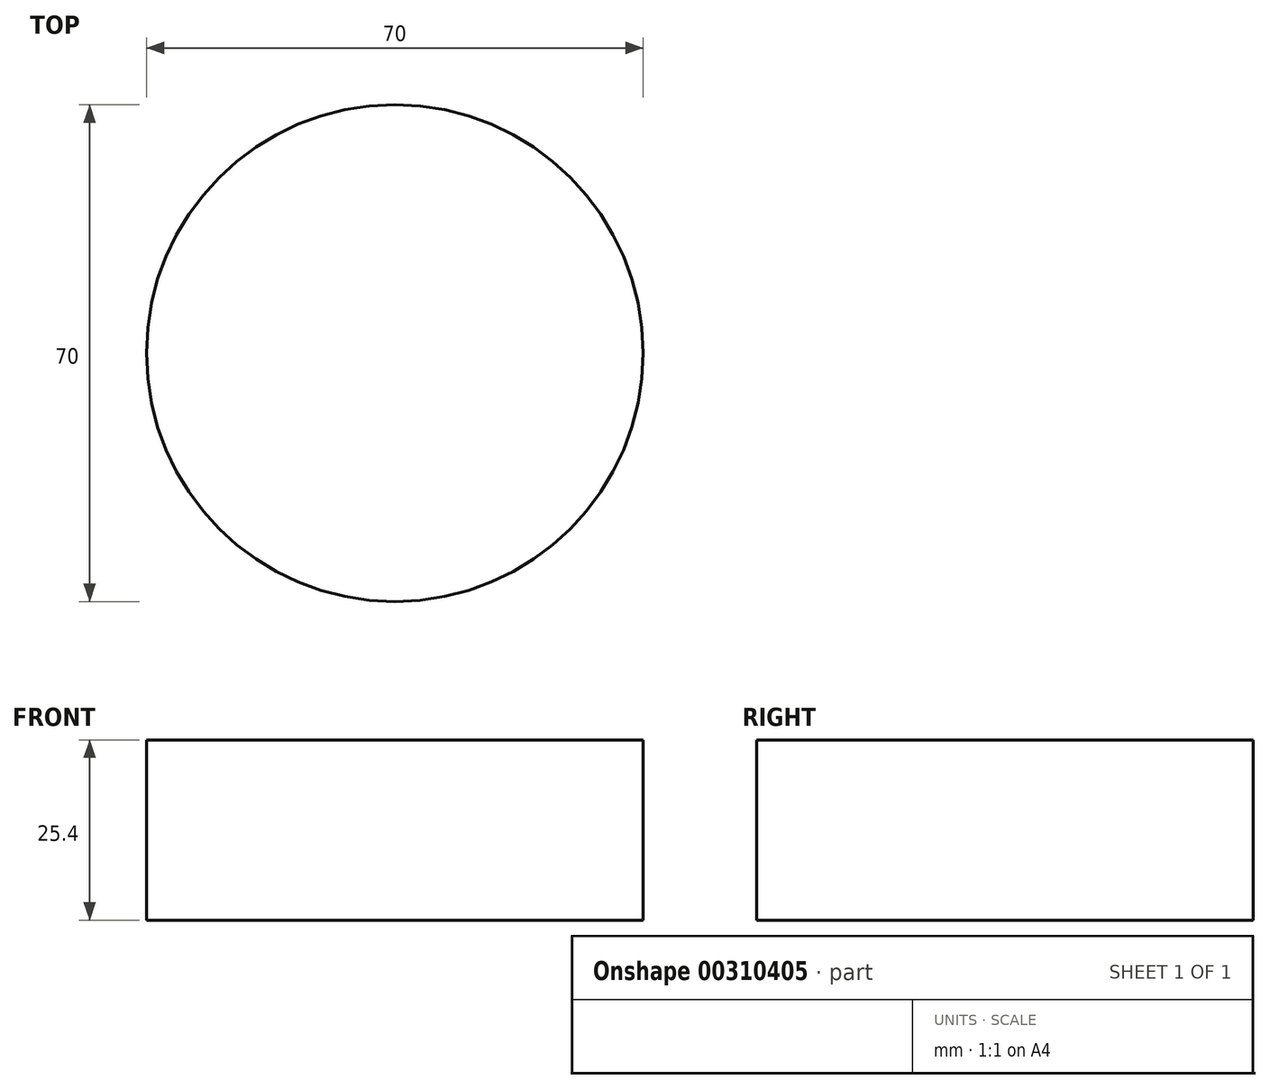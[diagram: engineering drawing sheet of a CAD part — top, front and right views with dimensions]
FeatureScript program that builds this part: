
annotation { "Feature Type Name" : "Feature", "Feature Type Description" : "" }
export const myFeature = defineFeature(function(context is Context, id is Id, definition is map)
    precondition{}
    {
        {
            var Q0;
            Q0=qCreatedBy(makeId("Top.planeOp"),FACE);
            var sketch = newSketch(context, id + "F0", { "sketchPlane" : qUnion([Q0])});
            skCircle(sketch, "E0", {"center": v(0, 0) * mm, "radius": 35 * mm});
            skSolve(sketch);
        }
        {
            var Q0;
            Q0=makeQuery(id+"F0.imprint","IMPRINT",FACE,{"disambiguationData":[TD([[makeQuery(id+"F0.imprint","IMPRINT",EDGE,{"derivedFrom":sQuery(id+"F0.wireOp",EDGE,"E0")}),1.0]])]});
            extrude(context, id + "F1", {"entities" : qUnion([Q0]), "depth" : 25.4 * mm, "offsetDistance" : 25.4 * mm});
        }
        {
            var Q0;
            Q0=makeQuery(id+"F1.opExtrude","CAP_FACE",FACE,{"disambiguationData":[OSD([sQuery(id+"F0.wireOp",EDGE,"E0")])],"isStart":false});
            extrude(context, id + "F2", {"entities" : qUnion([Q0]), "operationType" : NewBodyOperationType.ADD, "oppositeDirection" : true, "depth" : 8 * mm, "offsetDistance" : 25.4 * mm});
        }
        {
            var Q0;
            Q0=makeQuery(id+"F1.opExtrude","CAP_FACE",FACE,{"disambiguationData":[OSD([sQuery(id+"F0.wireOp",EDGE,"E0")])],"isStart":false});
            extrude(context, id + "F3", {"entities" : qUnion([Q0]), "operationType" : NewBodyOperationType.ADD, "oppositeDirection" : true, "depth" : 10 * mm, "offsetDistance" : 25.4 * mm});
        }
    });
